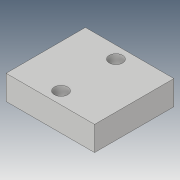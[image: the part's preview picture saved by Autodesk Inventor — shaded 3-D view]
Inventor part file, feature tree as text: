
AUTODESK INVENTOR PART (.ipt)
format: ipt  version: 2019 (Build 230136000, 136)  size: 91,648 bytes
history: native  units: mm
features: extrude x2, sketch x2
ambient origin geometry x8: Origin, YZ Plane, XZ Plane, XY Plane, X Axis, Y Axis, Z Axis, Center Point
bodies: Solid1 (feature_tree)
feature tree (4):
  extrude  "Extrusion1"  Depth=13.0mm
  extrude  "Extrusion2"  Depth=3.0mm
  sketch  "Sketch1"  dims[d0=14.5mm d1=13.0mm]
  sketch  "Sketch2"  dims[d2=4.0mm d3=0.0mm d4=2.2mm d5=2.2mm d6=2.0mm d7=7.0mm d8=7.0mm d9=2.0mm d10=3.0mm d11=0.0mm]
